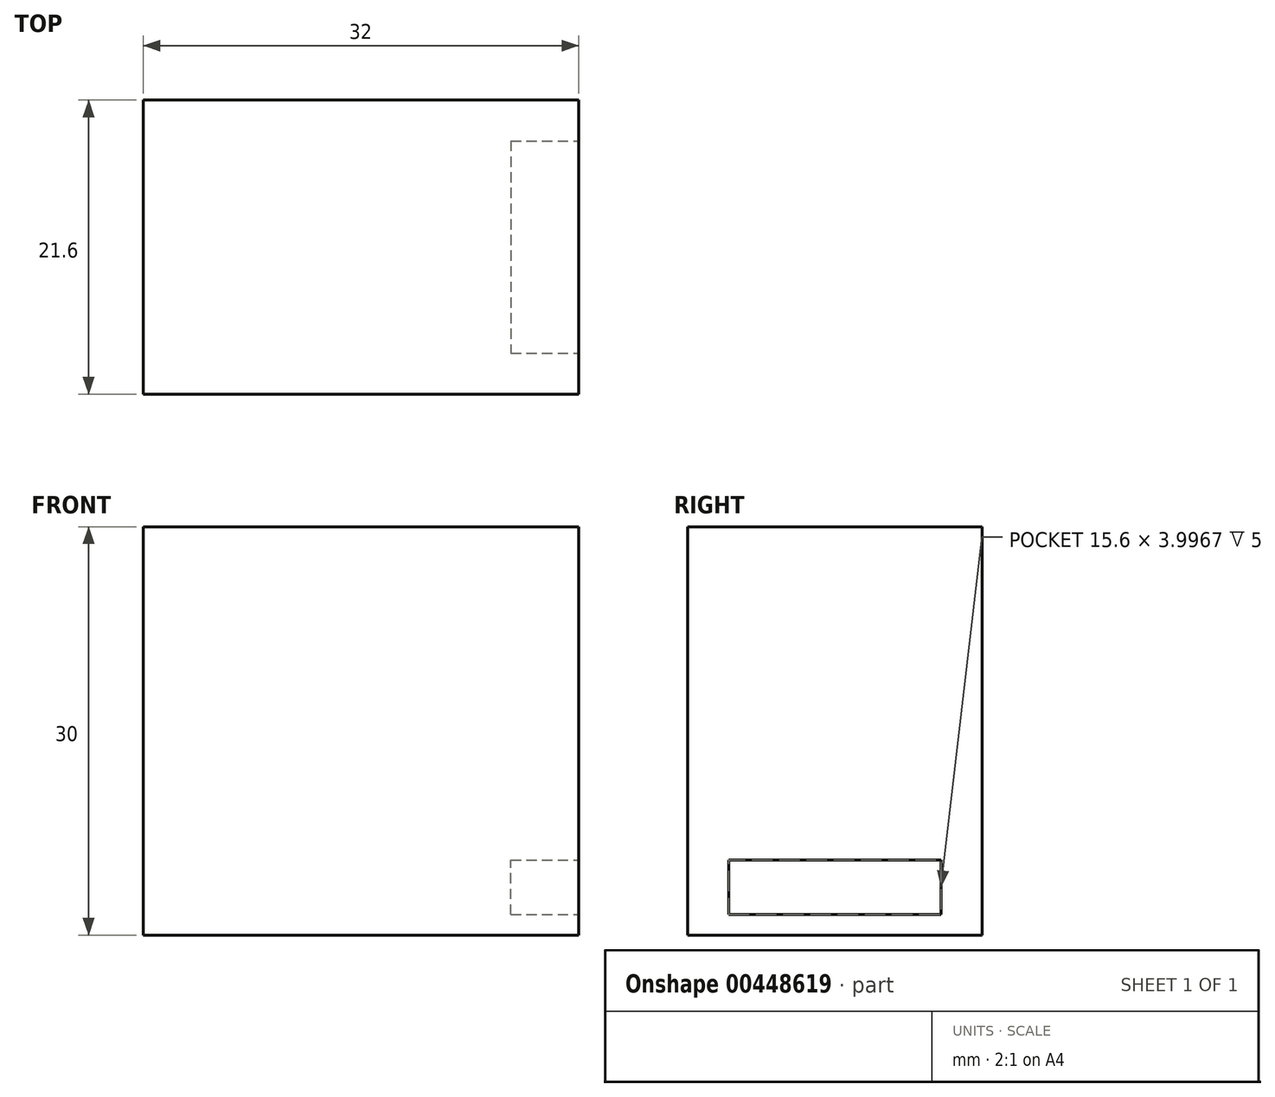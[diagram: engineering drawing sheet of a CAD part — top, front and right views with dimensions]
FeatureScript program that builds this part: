
annotation { "Feature Type Name" : "Feature", "Feature Type Description" : "" }
export const myFeature = defineFeature(function(context is Context, id is Id, definition is map)
    precondition{}
    {
        {
            var Q0;
            Q0=qCreatedBy(makeId("Top.planeOp"),FACE);
            var sketch = newSketch(context, id + "F0", { "sketchPlane" : qUnion([Q0])});
            skLineSegment(sketch, "E0.bottom", {"start": v(16, -10.8) * mm, "end": v(-16, -10.8) * mm});
            skLineSegment(sketch, "E0.top", {"start": v(16, 10.8) * mm, "end": v(-16, 10.8) * mm});
            skLineSegment(sketch, "E0.left", {"start": v(16, -10.8) * mm, "end": v(16, 10.8) * mm});
            skLineSegment(sketch, "E0.right", {"start": v(-16, -10.8) * mm, "end": v(-16, 10.8) * mm});
            skPoint(sketch, "E0.middle", {"position": v(0, 0) * mm});
            skSolve(sketch);
        }
        {
            var Q0;
            Q0=makeQuery(id+"F0.imprint","IMPRINT",FACE,{"disambiguationData":[TD([[makeQuery(id+"F0.imprint","IMPRINT",EDGE,{"derivedFrom":sQuery(id+"F0.wireOp",EDGE,"E0.bottom")}),-1.0]])]});
            extrude(context, id + "F1", {"entities" : qUnion([Q0]), "depth" : 30 * mm});
        }
        {
            var Q0;
            Q0=makeQuery(id+"F1.opExtrude","SWEPT_FACE",FACE,{"disambiguationData":[OSD([sQuery(id+"F0.wireOp",EDGE,"E0.left")])]});
            var sketch = newSketch(context, id + "F2", { "sketchPlane" : qUnion([Q0])});
            skLineSegment(sketch, "E1.bottom", {"start": v(-10.8, 0) * mm, "end": v(10.8, 0) * mm});
            skLineSegment(sketch, "E1.top", {"start": v(-10.8, 5.5) * mm, "end": v(10.8, 5.5) * mm});
            skLineSegment(sketch, "E1.left", {"start": v(-10.8, 0) * mm, "end": v(-10.8, 5.5) * mm});
            skLineSegment(sketch, "E1.right", {"start": v(10.8, 0) * mm, "end": v(10.8, 5.5) * mm});
            skSolve(sketch);
        }
        {
            var Q0;
            {var subQ0=sQuery(id+"F2.wireOp",EDGE,"E1.top");Q0=makeQuery(id+"F2.imprint","IMPRINT",FACE,{"disambiguationData":[TD([[makeQuery(id+"F2.imprint","IMPRINT",EDGE,{"derivedFrom":subQ0}),1.0]])]});}
            var sketch = newSketch(context, id + "F3", { "sketchPlane" : qUnion([Q0])});
            skLineSegment(sketch, "E2.bottom", {"start": v(7.8, 1.5) * mm, "end": v(-7.8, 1.5) * mm});
            skLineSegment(sketch, "E2.top", {"start": v(7.8, 5.5) * mm, "end": v(-7.8, 5.5) * mm});
            skLineSegment(sketch, "E2.left", {"start": v(7.8, 1.5) * mm, "end": v(7.8, 5.5) * mm});
            skLineSegment(sketch, "E2.right", {"start": v(-7.8, 1.5) * mm, "end": v(-7.8, 5.5) * mm});
            skSolve(sketch);
        }
        {
            var Q0;
            Q0 = qSketchRegion(id + "F3", true);
            extrude(context, id + "F4", {"entities" : qUnion([Q0]), "operationType" : NewBodyOperationType.REMOVE, "oppositeDirection" : true, "depth" : 5 * mm});
        }
    });
